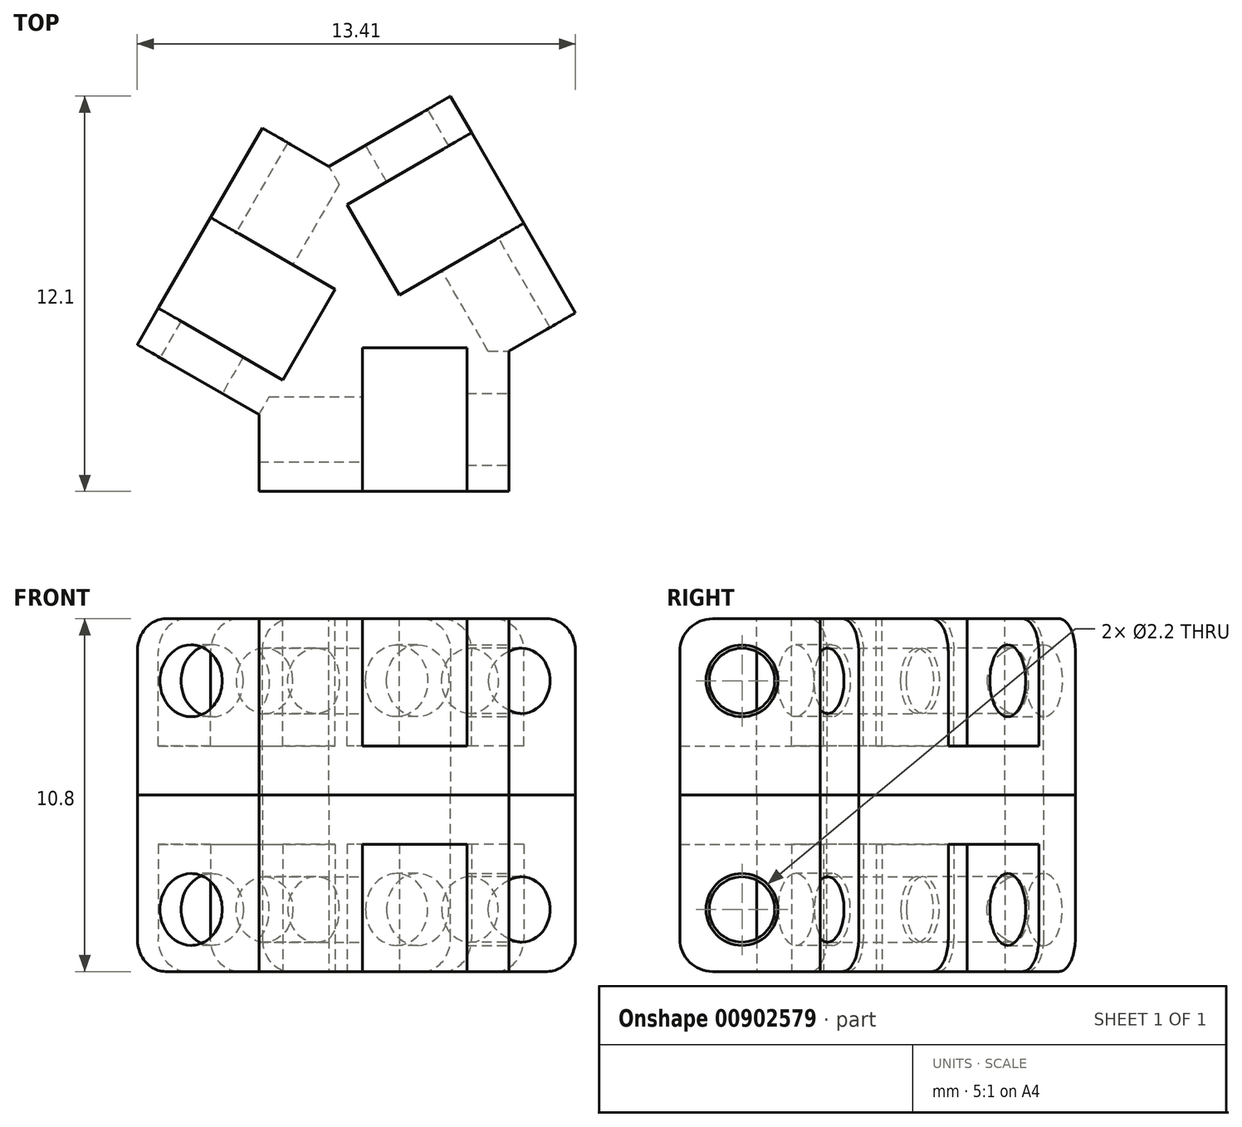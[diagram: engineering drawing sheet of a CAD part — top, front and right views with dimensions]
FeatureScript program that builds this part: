
annotation { "Feature Type Name" : "Feature", "Feature Type Description" : "" }
export const myFeature = defineFeature(function(context is Context, id is Id, definition is map)
    precondition{}
    {
        {
            var Q0;
            Q0=qCreatedBy(makeId("Top.planeOp"),FACE);
            var sketch = newSketch(context, id + "F0", { "sketchPlane" : qUnion([Q0])});
            skLineSegment(sketch, "E0", {"start": v(-2.25, 6.37) * mm, "end": v(-6.64, -1.24) * mm});
            skLineSegment(sketch, "E1", {"start": v(-6.64, -1.24) * mm, "end": v(-4.39, -5.13) * mm});
            skLineSegment(sketch, "E2", {"start": v(-4.39, -5.13) * mm, "end": v(4.39, -5.13) * mm});
            skLineSegment(sketch, "E3", {"start": v(4.39, -5.13) * mm, "end": v(6.64, -1.24) * mm});
            skLineSegment(sketch, "E4", {"start": v(6.64, -1.24) * mm, "end": v(2.25, 6.37) * mm});
            skLineSegment(sketch, "E5", {"start": v(2.25, 6.37) * mm, "end": v(-2.25, 6.37) * mm});
            skLineSegment(sketch, "E6", {"start": v(-5.51, -3.18) * mm, "end": v(4.44, 2.57) * mm, "construction": true});
            skLineSegment(sketch, "E7", {"start": v(0, 6.37) * mm, "end": v(0, -5.13) * mm, "construction": true});
            skSolve(sketch);
        }
        {
            var Q0;
            Q0 = qSketchRegion(id + "F0", true);
            extrude(context, id + "F1", {"entities" : qUnion([Q0]), "depth" : 5 * mm, "offsetDistance" : 25 * mm});
        }
        {
            var Q0;
            Q0=makeQuery(id+"F1.opExtrude","CAP_FACE",FACE,{"disambiguationData":[OSD([sQuery(id+"F0.wireOp",EDGE,"E0"),sQuery(id+"F0.wireOp",EDGE,"E1"),sQuery(id+"F0.wireOp",EDGE,"E2"),sQuery(id+"F0.wireOp",EDGE,"E3"),sQuery(id+"F0.wireOp",EDGE,"E4"),sQuery(id+"F0.wireOp",EDGE,"E5")])],"isStart":false});
            var sketch = newSketch(context, id + "F2", { "sketchPlane" : qUnion([Q0])});
            skLineSegment(sketch, "E8.bottom", {"start": v(-0.1, -5.13) * mm, "end": v(3.1, -5.13) * mm});
            skLineSegment(sketch, "E8.top", {"start": v(-0.1, -1.13) * mm, "end": v(3.1, -1.13) * mm});
            skLineSegment(sketch, "E8.left", {"start": v(-0.1, -5.13) * mm, "end": v(-0.1, -1.13) * mm});
            skLineSegment(sketch, "E8.right", {"start": v(3.1, -5.13) * mm, "end": v(3.1, -1.13) * mm});
            skPoint(sketch, "E9", {"position": v(1.5, -5.13) * mm});
            skLineSegment(sketch, "E10.1.0", {"start": v(2.9, 5.25) * mm, "end": v(-0.57, 3.25) * mm});
            skLineSegment(sketch, "E10.1.1", {"start": v(1.03, 0.48) * mm, "end": v(-0.57, 3.25) * mm});
            skLineSegment(sketch, "E10.1.2", {"start": v(4.5, 2.48) * mm, "end": v(1.03, 0.48) * mm});
            skLineSegment(sketch, "E10.1.3", {"start": v(4.5, 2.48) * mm, "end": v(2.9, 5.25) * mm});
            skLineSegment(sketch, "E10.2.0", {"start": v(-6, -0.12) * mm, "end": v(-2.53, -2.12) * mm});
            skLineSegment(sketch, "E10.2.1", {"start": v(-0.93, 0.65) * mm, "end": v(-2.53, -2.12) * mm});
            skLineSegment(sketch, "E10.2.2", {"start": v(-4.4, 2.65) * mm, "end": v(-0.93, 0.65) * mm});
            skLineSegment(sketch, "E10.2.3", {"start": v(-4.4, 2.65) * mm, "end": v(-6, -0.12) * mm});
            skPoint(sketch, "E10.center", {"position": v(0, 0) * mm});
            skSolve(sketch);
        }
        {
            var Q0;
            Q0 = qSketchRegion(id + "F2", true);
            extrude(context, id + "F3", {"entities" : qUnion([Q0]), "operationType" : NewBodyOperationType.REMOVE, "oppositeDirection" : true, "depth" : 3.5 * mm, "offsetDistance" : 25 * mm});
        }
        {
            var Q0;
            Q0=makeQuery(id+"F1.opExtrude","CAP_FACE",FACE,{"disambiguationData":[OSD([sQuery(id+"F0.wireOp",EDGE,"E0"),sQuery(id+"F0.wireOp",EDGE,"E1"),sQuery(id+"F0.wireOp",EDGE,"E2"),sQuery(id+"F0.wireOp",EDGE,"E3"),sQuery(id+"F0.wireOp",EDGE,"E4"),sQuery(id+"F0.wireOp",EDGE,"E5")])],"isStart":false});
            var sketch = newSketch(context, id + "F4", { "sketchPlane" : qUnion([Q0])});
            skLineSegment(sketch, "E11.bottom", {"start": v(4.39, -5.13) * mm, "end": v(6.64, -5.13) * mm});
            skLineSegment(sketch, "E11.top", {"start": v(4.39, -1.24) * mm, "end": v(6.64, -1.24) * mm});
            skLineSegment(sketch, "E11.left", {"start": v(4.39, -5.13) * mm, "end": v(4.39, -1.24) * mm});
            skLineSegment(sketch, "E11.right", {"start": v(6.64, -5.13) * mm, "end": v(6.64, -1.24) * mm});
            skLineSegment(sketch, "E12.1.0", {"start": v(2.25, 6.37) * mm, "end": v(1.12, 8.32) * mm});
            skLineSegment(sketch, "E12.1.1", {"start": v(-1.12, 4.42) * mm, "end": v(-2.25, 6.37) * mm});
            skLineSegment(sketch, "E12.1.2", {"start": v(2.25, 6.37) * mm, "end": v(-1.13, 4.42) * mm});
            skLineSegment(sketch, "E12.1.3", {"start": v(1.13, 8.32) * mm, "end": v(-2.25, 6.37) * mm});
            skLineSegment(sketch, "E12.2.0", {"start": v(-6.64, -1.24) * mm, "end": v(-7.76, -3.18) * mm});
            skLineSegment(sketch, "E12.2.1", {"start": v(-3.26, -3.18) * mm, "end": v(-4.39, -5.13) * mm});
            skLineSegment(sketch, "E12.2.2", {"start": v(-6.64, -1.24) * mm, "end": v(-3.26, -3.18) * mm});
            skLineSegment(sketch, "E12.2.3", {"start": v(-7.76, -3.18) * mm, "end": v(-4.39, -5.13) * mm});
            skPoint(sketch, "E12.center", {"position": v(0, 0) * mm});
            skSolve(sketch);
        }
        {
            var Q0;
            Q0 = qSketchRegion(id + "F4", true);
            var Q1;
            Q1=makeQuery(id+"F1.opExtrude","CAP_FACE",FACE,{"disambiguationData":[OSD([sQuery(id+"F0.wireOp",EDGE,"E0"),sQuery(id+"F0.wireOp",EDGE,"E1"),sQuery(id+"F0.wireOp",EDGE,"E2"),sQuery(id+"F0.wireOp",EDGE,"E3"),sQuery(id+"F0.wireOp",EDGE,"E4"),sQuery(id+"F0.wireOp",EDGE,"E5")])],"isStart":true});
            extrude(context, id + "F5", {"entities" : qUnion([Q0]), "operationType" : NewBodyOperationType.REMOVE, "endBound" : BoundingType.UP_TO_SURFACE, "oppositeDirection" : true, "depth" : 25 * mm, "endBoundEntityFace" : qUnion([Q1]), "offsetDistance" : 25 * mm});
        }
        {
            var Q0;
            Q0=makeQuery(id+"F5.boolean.opBoolean","COPY",FACE,{"derivedFrom":makeQuery(id+"F5.opExtrude","SWEPT_FACE",FACE,{"disambiguationData":[OSD([sQuery(id+"F4.wireOp",EDGE,"E12.2.2")])]})});
            var sketch = newSketch(context, id + "F6", { "sketchPlane" : qUnion([Q0])});
            skCircle(sketch, "E13", {"center": v(-3.63, 3.5) * mm, "radius": 1.1 * mm});
            skSolve(sketch);
        }
        {
            var Q0;
            Q0=makeQuery(id+"F5.boolean.opBoolean","COPY",FACE,{"derivedFrom":makeQuery(id+"F5.opExtrude","SWEPT_FACE",FACE,{"disambiguationData":[OSD([sQuery(id+"F4.wireOp",EDGE,"E11.left")])]})});
            var sketch = newSketch(context, id + "F7", { "sketchPlane" : qUnion([Q0])});
            skCircle(sketch, "E14", {"center": v(-3.63, 3.5) * mm, "radius": 1.1 * mm});
            skSolve(sketch);
        }
        {
            var Q0;
            Q0=makeQuery(id+"F6.imprint","IMPRINT",FACE,{"disambiguationData":[TD([[makeQuery(id+"F6.imprint","IMPRINT",EDGE,{"derivedFrom":sQuery(id+"F6.wireOp",EDGE,"E13")}),1.0]])]});
            var Q1;
            Q1=makeQuery(id+"F3.boolean.opBoolean","COPY",FACE,{"derivedFrom":makeQuery(id+"F3.opExtrude","SWEPT_FACE",FACE,{"disambiguationData":[OSD([sQuery(id+"F2.wireOp",EDGE,"E10.2.0")])]})});
            extrude(context, id + "F8", {"entities" : qUnion([Q0]), "operationType" : NewBodyOperationType.REMOVE, "endBound" : BoundingType.UP_TO_SURFACE, "oppositeDirection" : true, "depth" : 25 * mm, "endBoundEntityFace" : qUnion([Q1]), "offsetDistance" : 25 * mm});
        }
        {
            var Q0;
            Q0=makeQuery(id+"F5.boolean.opBoolean","COPY",FACE,{"derivedFrom":makeQuery(id+"F5.opExtrude","SWEPT_FACE",FACE,{"disambiguationData":[OSD([sQuery(id+"F4.wireOp",EDGE,"E12.1.2")])]})});
            var sketch = newSketch(context, id + "F9", { "sketchPlane" : qUnion([Q0])});
            skCircle(sketch, "E15", {"center": v(-3.63, 3.5) * mm, "radius": 1.1 * mm});
            skSolve(sketch);
        }
        {
            var Q0;
            Q0 = qSketchRegion(id + "F7", true);
            var Q1;
            Q1=makeQuery(id+"F3.boolean.opBoolean","COPY",FACE,{"derivedFrom":makeQuery(id+"F3.opExtrude","SWEPT_FACE",FACE,{"disambiguationData":[OSD([sQuery(id+"F2.wireOp",EDGE,"E8.right")])]})});
            extrude(context, id + "F10", {"entities" : qUnion([Q0]), "operationType" : NewBodyOperationType.REMOVE, "endBound" : BoundingType.UP_TO_SURFACE, "oppositeDirection" : true, "depth" : 25 * mm, "endBoundEntityFace" : qUnion([Q1]), "offsetDistance" : 25 * mm});
        }
        {
            var Q0;
            Q0 = qSketchRegion(id + "F9", true);
            var Q1;
            Q1=makeQuery(id+"F3.boolean.opBoolean","COPY",FACE,{"derivedFrom":makeQuery(id+"F3.opExtrude","SWEPT_FACE",FACE,{"disambiguationData":[OSD([sQuery(id+"F2.wireOp",EDGE,"E10.1.0")])]})});
            extrude(context, id + "F11", {"entities" : qUnion([Q0]), "operationType" : NewBodyOperationType.REMOVE, "endBound" : BoundingType.UP_TO_SURFACE, "oppositeDirection" : true, "depth" : 25 * mm, "endBoundEntityFace" : qUnion([Q1]), "offsetDistance" : 25 * mm});
        }
        {
            var Q0;
            Q0=makeQuery(id+"F3.boolean.opBoolean","COPY",FACE,{"derivedFrom":makeQuery(id+"F3.opExtrude","SWEPT_FACE",FACE,{"disambiguationData":[OSD([sQuery(id+"F2.wireOp",EDGE,"E8.left")])]})});
            var sketch = newSketch(context, id + "F12", { "sketchPlane" : qUnion([Q0])});
            skCircle(sketch, "E16", {"center": v(-3.63, 3.5) * mm, "radius": 1 * mm});
            skSolve(sketch);
        }
        {
            var Q0;
            Q0=makeQuery(id+"F3.boolean.opBoolean","COPY",FACE,{"derivedFrom":makeQuery(id+"F3.opExtrude","SWEPT_FACE",FACE,{"disambiguationData":[OSD([sQuery(id+"F2.wireOp",EDGE,"E10.1.2")])]})});
            var sketch = newSketch(context, id + "F13", { "sketchPlane" : qUnion([Q0])});
            skCircle(sketch, "E17", {"center": v(-3.63, 3.5) * mm, "radius": 1 * mm});
            skSolve(sketch);
        }
        {
            var Q0;
            Q0=makeQuery(id+"F3.boolean.opBoolean","COPY",FACE,{"derivedFrom":makeQuery(id+"F3.opExtrude","SWEPT_FACE",FACE,{"disambiguationData":[OSD([sQuery(id+"F2.wireOp",EDGE,"E10.2.2")])]})});
            var sketch = newSketch(context, id + "F14", { "sketchPlane" : qUnion([Q0])});
            skCircle(sketch, "E18", {"center": v(-3.63, 3.5) * mm, "radius": 1 * mm});
            skSolve(sketch);
        }
        {
            var Q0;
            Q0 = qSketchRegion(id + "F12", true);
            var Q1;
            Q1=makeQuery(id+"F5.boolean.opBoolean","COPY",FACE,{"derivedFrom":makeQuery(id+"F5.opExtrude","SWEPT_FACE",FACE,{"disambiguationData":[OSD([sQuery(id+"F4.wireOp",EDGE,"E12.2.1")])]})});
            extrude(context, id + "F15", {"entities" : qUnion([Q0]), "operationType" : NewBodyOperationType.REMOVE, "endBound" : BoundingType.UP_TO_SURFACE, "oppositeDirection" : true, "depth" : 25 * mm, "endBoundEntityFace" : qUnion([Q1]), "offsetDistance" : 25 * mm});
        }
        {
            var Q0;
            Q0 = qSketchRegion(id + "F13", true);
            var Q1;
            Q1=makeQuery(id+"F5.boolean.opBoolean","COPY",FACE,{"derivedFrom":makeQuery(id+"F5.opExtrude","SWEPT_FACE",FACE,{"disambiguationData":[OSD([sQuery(id+"F4.wireOp",EDGE,"E11.top")])]})});
            extrude(context, id + "F16", {"entities" : qUnion([Q0]), "operationType" : NewBodyOperationType.REMOVE, "endBound" : BoundingType.UP_TO_SURFACE, "oppositeDirection" : true, "depth" : 25 * mm, "endBoundEntityFace" : qUnion([Q1]), "offsetDistance" : 25 * mm});
        }
        {
            var Q0;
            Q0 = qSketchRegion(id + "F14", true);
            var Q1;
            Q1=makeQuery(id+"F5.boolean.opBoolean","COPY",FACE,{"derivedFrom":makeQuery(id+"F5.opExtrude","SWEPT_FACE",FACE,{"disambiguationData":[OSD([sQuery(id+"F4.wireOp",EDGE,"E12.1.1")])]})});
            extrude(context, id + "F17", {"entities" : qUnion([Q0]), "operationType" : NewBodyOperationType.REMOVE, "endBound" : BoundingType.UP_TO_SURFACE, "oppositeDirection" : true, "depth" : 25 * mm, "endBoundEntityFace" : qUnion([Q1]), "offsetDistance" : 25 * mm});
        }
        {
            var Q0;
            Q0=makeQuery(id+"F1.opExtrude","CAP_FACE",FACE,{"disambiguationData":[OSD([sQuery(id+"F0.wireOp",EDGE,"E0"),sQuery(id+"F0.wireOp",EDGE,"E1"),sQuery(id+"F0.wireOp",EDGE,"E2"),sQuery(id+"F0.wireOp",EDGE,"E3"),sQuery(id+"F0.wireOp",EDGE,"E4"),sQuery(id+"F0.wireOp",EDGE,"E5")])],"isStart":false});
            extrude(context, id + "F18", {"entities" : qUnion([Q0]), "operationType" : NewBodyOperationType.ADD, "depth" : 0.4 * mm, "offsetDistance" : 25 * mm});
        }
        {
            var Q0;
            {var subQ0=sQuery(id+"F0.wireOp",EDGE,"E5");var subQ1=sQuery(id+"F0.wireOp",EDGE,"E4");var subQ2=sQuery(id+"F0.wireOp",EDGE,"E3");var subQ4=makeQuery(id+"F1.opExtrude","SWEPT_FACE",FACE,{"disambiguationData":[OSD([subQ1])]});var subQ5=makeQuery(id+"F1.opExtrude","CAP_EDGE",EDGE,{"disambiguationData":[OSD([subQ1])],"isStart":false});Q0=makeQuery(id+"F18.boolean.opBoolean","MERGE",FACE,{"derivedFrom":[subQ4,makeQuery(id+"F18.opExtrude","SWEPT_FACE",FACE,{"disambiguationData":[OSD([subQ1]),TDD([makeQuery(id+"F3.boolean.opBoolean","SPLIT",EDGE,{"disambiguationData":[TD([makeQuery(id+"F1.opExtrude","SWEPT_FACE",FACE,{"disambiguationData":[OSD([subQ2])]})])],"derivedFrom":subQ5})])]}),makeQuery(id+"F18.opExtrude","SWEPT_FACE",FACE,{"disambiguationData":[OSD([subQ1]),TDD([makeQuery(id+"F3.boolean.opBoolean","SPLIT",EDGE,{"disambiguationData":[TD([makeQuery(id+"F1.opExtrude","SWEPT_FACE",FACE,{"disambiguationData":[OSD([subQ0])]})])],"derivedFrom":subQ5})])]})]});}
            extrude(context, id + "F19", {"entities" : qUnion([Q0]), "operationType" : NewBodyOperationType.ADD, "depth" : 0.4 * mm, "offsetDistance" : 25 * mm});
        }
        {
            var Q0;
            {var subQ0=sQuery(id+"F0.wireOp",EDGE,"E0");var subQ1=makeQuery(id+"F1.opExtrude","SWEPT_FACE",FACE,{"disambiguationData":[OSD([subQ0])]});var subQ2=sQuery(id+"F0.wireOp",EDGE,"E5");var subQ3=sQuery(id+"F0.wireOp",EDGE,"E1");var subQ5=makeQuery(id+"F1.opExtrude","CAP_EDGE",EDGE,{"disambiguationData":[OSD([subQ0])],"isStart":false});Q0=makeQuery(id+"F18.boolean.opBoolean","MERGE",FACE,{"derivedFrom":[subQ1,makeQuery(id+"F18.opExtrude","SWEPT_FACE",FACE,{"disambiguationData":[OSD([subQ0]),TDD([makeQuery(id+"F3.boolean.opBoolean","SPLIT",EDGE,{"disambiguationData":[TD([makeQuery(id+"F1.opExtrude","SWEPT_FACE",FACE,{"disambiguationData":[OSD([subQ2])]})])],"derivedFrom":subQ5})])]}),makeQuery(id+"F18.opExtrude","SWEPT_FACE",FACE,{"disambiguationData":[OSD([subQ0]),TDD([makeQuery(id+"F3.boolean.opBoolean","SPLIT",EDGE,{"disambiguationData":[TD([makeQuery(id+"F1.opExtrude","SWEPT_FACE",FACE,{"disambiguationData":[OSD([subQ3])]})])],"derivedFrom":subQ5})])]})]});}
            extrude(context, id + "F20", {"entities" : qUnion([Q0]), "operationType" : NewBodyOperationType.ADD, "depth" : 0.4 * mm, "offsetDistance" : 25 * mm});
        }
        {
            var Q0;
            {var subQ0=sQuery(id+"F0.wireOp",EDGE,"E3");var subQ1=sQuery(id+"F0.wireOp",EDGE,"E2");var subQ2=sQuery(id+"F0.wireOp",EDGE,"E1");var subQ4=makeQuery(id+"F1.opExtrude","SWEPT_FACE",FACE,{"disambiguationData":[OSD([subQ1])]});var subQ5=makeQuery(id+"F1.opExtrude","CAP_EDGE",EDGE,{"disambiguationData":[OSD([subQ1])],"isStart":false});Q0=makeQuery(id+"F18.boolean.opBoolean","MERGE",FACE,{"derivedFrom":[subQ4,makeQuery(id+"F18.opExtrude","SWEPT_FACE",FACE,{"disambiguationData":[OSD([subQ1]),TDD([makeQuery(id+"F3.boolean.opBoolean","SPLIT",EDGE,{"disambiguationData":[TD([makeQuery(id+"F1.opExtrude","SWEPT_FACE",FACE,{"disambiguationData":[OSD([subQ2])]})])],"derivedFrom":subQ5})])]}),makeQuery(id+"F18.opExtrude","SWEPT_FACE",FACE,{"disambiguationData":[OSD([subQ1]),TDD([makeQuery(id+"F3.boolean.opBoolean","SPLIT",EDGE,{"disambiguationData":[TD([makeQuery(id+"F1.opExtrude","SWEPT_FACE",FACE,{"disambiguationData":[OSD([subQ0])]})])],"derivedFrom":subQ5})])]})]});}
            extrude(context, id + "F21", {"entities" : qUnion([Q0]), "operationType" : NewBodyOperationType.ADD, "depth" : 0.4 * mm, "offsetDistance" : 25 * mm});
        }
        {
            var Q0;
            {var subQ0=sQuery(id+"F0.wireOp",EDGE,"E5");var subQ1=sQuery(id+"F0.wireOp",EDGE,"E4");var subQ2=sQuery(id+"F0.wireOp",EDGE,"E3");var subQ3=sQuery(id+"F0.wireOp",EDGE,"E2");var subQ4=sQuery(id+"F0.wireOp",EDGE,"E1");var subQ5=sQuery(id+"F0.wireOp",EDGE,"E0");var subQ8=makeQuery(id+"F1.opExtrude","SWEPT_FACE",FACE,{"disambiguationData":[OSD([subQ2])]});var subQ9=makeQuery(id+"F1.opExtrude","CAP_EDGE",EDGE,{"disambiguationData":[OSD([subQ3])],"isStart":false});var subQ10=makeQuery(id+"F1.opExtrude","SWEPT_FACE",FACE,{"disambiguationData":[OSD([subQ4])]});var subQ12=makeQuery(id+"F1.opExtrude","CAP_EDGE",EDGE,{"disambiguationData":[OSD([subQ5])],"isStart":false});var subQ13=makeQuery(id+"F1.opExtrude","SWEPT_FACE",FACE,{"disambiguationData":[OSD([subQ0])]});var subQ15=makeQuery(id+"F1.opExtrude","CAP_EDGE",EDGE,{"disambiguationData":[OSD([subQ1])],"isStart":false});Q0=makeQuery(id+"F21.boolean.opBoolean","MERGE",FACE,{"derivedFrom":[makeQuery(id+"F20.boolean.opBoolean","MERGE",FACE,{"derivedFrom":[makeQuery(id+"F19.boolean.opBoolean","MERGE",FACE,{"derivedFrom":[makeQuery(id+"F18.opExtrude","CAP_FACE",FACE,{"disambiguationData":[OSD([subQ5,subQ4,subQ3,subQ2,subQ1,subQ0])],"isStart":false}),makeQuery(id+"F19.opExtrude","SWEPT_FACE",FACE,{"disambiguationData":[OSD([subQ1]),TDD([makeQuery(id+"F18.opExtrude","CAP_EDGE",EDGE,{"disambiguationData":[OSD([subQ1]),TDD([makeQuery(id+"F3.boolean.opBoolean","SPLIT",EDGE,{"disambiguationData":[TD([subQ8])],"derivedFrom":subQ15})])],"isStart":false})])]}),makeQuery(id+"F19.opExtrude","SWEPT_FACE",FACE,{"disambiguationData":[OSD([subQ1]),TDD([makeQuery(id+"F18.opExtrude","CAP_EDGE",EDGE,{"disambiguationData":[OSD([subQ1]),TDD([makeQuery(id+"F3.boolean.opBoolean","SPLIT",EDGE,{"disambiguationData":[TD([subQ13])],"derivedFrom":subQ15})])],"isStart":false})])]})]}),makeQuery(id+"F20.opExtrude","SWEPT_FACE",FACE,{"disambiguationData":[OSD([subQ5]),TDD([makeQuery(id+"F18.opExtrude","CAP_EDGE",EDGE,{"disambiguationData":[OSD([subQ5]),TDD([makeQuery(id+"F3.boolean.opBoolean","SPLIT",EDGE,{"disambiguationData":[TD([subQ13])],"derivedFrom":subQ12})])],"isStart":false})])]}),makeQuery(id+"F20.opExtrude","SWEPT_FACE",FACE,{"disambiguationData":[OSD([subQ5]),TDD([makeQuery(id+"F18.opExtrude","CAP_EDGE",EDGE,{"disambiguationData":[OSD([subQ5]),TDD([makeQuery(id+"F3.boolean.opBoolean","SPLIT",EDGE,{"disambiguationData":[TD([subQ10])],"derivedFrom":subQ12})])],"isStart":false})])]})]}),makeQuery(id+"F21.opExtrude","SWEPT_FACE",FACE,{"disambiguationData":[OSD([subQ3]),TDD([makeQuery(id+"F18.opExtrude","CAP_EDGE",EDGE,{"disambiguationData":[OSD([subQ3]),TDD([makeQuery(id+"F3.boolean.opBoolean","SPLIT",EDGE,{"disambiguationData":[TD([subQ10])],"derivedFrom":subQ9})])],"isStart":false})])]}),makeQuery(id+"F21.opExtrude","SWEPT_FACE",FACE,{"disambiguationData":[OSD([subQ3]),TDD([makeQuery(id+"F18.opExtrude","CAP_EDGE",EDGE,{"disambiguationData":[OSD([subQ3]),TDD([makeQuery(id+"F3.boolean.opBoolean","SPLIT",EDGE,{"disambiguationData":[TD([subQ8])],"derivedFrom":subQ9})])],"isStart":false})])]})]});}
            var sketch = newSketch(context, id + "F22", { "sketchPlane" : qUnion([Q0])});
            skLineSegment(sketch, "E19.bottom", {"start": v(-3.26, -3.18) * mm, "end": v(-4.39, -3.18) * mm});
            skLineSegment(sketch, "E19.top", {"start": v(-3.26, -5.53) * mm, "end": v(-4.39, -5.53) * mm});
            skLineSegment(sketch, "E19.left", {"start": v(-3.26, -3.18) * mm, "end": v(-3.26, -5.53) * mm});
            skLineSegment(sketch, "E19.right", {"start": v(-4.39, -3.18) * mm, "end": v(-4.39, -5.53) * mm});
            skLineSegment(sketch, "E20.1.0", {"start": v(4.39, -1.24) * mm, "end": v(4.95, -2.2) * mm});
            skLineSegment(sketch, "E20.1.1", {"start": v(4.95, -2.2) * mm, "end": v(6.99, -1.04) * mm});
            skLineSegment(sketch, "E20.1.2", {"start": v(4.39, -1.24) * mm, "end": v(6.42, -0.06) * mm});
            skLineSegment(sketch, "E20.1.3", {"start": v(6.42, -0.06) * mm, "end": v(6.99, -1.04) * mm});
            skLineSegment(sketch, "E20.2.0", {"start": v(-1.12, 4.42) * mm, "end": v(-0.56, 5.4) * mm});
            skLineSegment(sketch, "E20.2.1", {"start": v(-0.56, 5.4) * mm, "end": v(-2.6, 6.57) * mm});
            skLineSegment(sketch, "E20.2.2", {"start": v(-1.12, 4.42) * mm, "end": v(-3.16, 5.6) * mm});
            skLineSegment(sketch, "E20.2.3", {"start": v(-3.16, 5.6) * mm, "end": v(-2.6, 6.57) * mm});
            skPoint(sketch, "E20.center", {"position": v(0, 0) * mm});
            skSolve(sketch);
        }
        {
            var Q0;
            Q0 = qSketchRegion(id + "F22", true);
            var Q1;
            {var subQ0=sQuery(id+"F0.wireOp",EDGE,"E2");var subQ1=sQuery(id+"F0.wireOp",EDGE,"E0");var subQ2=sQuery(id+"F0.wireOp",EDGE,"E4");Q1=makeQuery(id+"F21.boolean.opBoolean","MERGE",FACE,{"derivedFrom":[makeQuery(id+"F20.boolean.opBoolean","MERGE",FACE,{"derivedFrom":[makeQuery(id+"F19.boolean.opBoolean","MERGE",FACE,{"derivedFrom":[makeQuery(id+"F1.opExtrude","CAP_FACE",FACE,{"disambiguationData":[OSD([subQ1,sQuery(id+"F0.wireOp",EDGE,"E1"),subQ0,sQuery(id+"F0.wireOp",EDGE,"E3"),subQ2,sQuery(id+"F0.wireOp",EDGE,"E5")])],"isStart":true}),makeQuery(id+"F19.opExtrude","SWEPT_FACE",FACE,{"disambiguationData":[OSD([subQ2]),TDD([makeQuery(id+"F1.opExtrude","CAP_EDGE",EDGE,{"disambiguationData":[OSD([subQ2])],"isStart":true})])]})]}),makeQuery(id+"F20.opExtrude","SWEPT_FACE",FACE,{"disambiguationData":[OSD([subQ1]),TDD([makeQuery(id+"F1.opExtrude","CAP_EDGE",EDGE,{"disambiguationData":[OSD([subQ1])],"isStart":true})])]})]}),makeQuery(id+"F21.opExtrude","SWEPT_FACE",FACE,{"disambiguationData":[OSD([subQ0]),TDD([makeQuery(id+"F1.opExtrude","CAP_EDGE",EDGE,{"disambiguationData":[OSD([subQ0])],"isStart":true})])]})]});}
            extrude(context, id + "F23", {"entities" : qUnion([Q0]), "operationType" : NewBodyOperationType.REMOVE, "endBound" : BoundingType.UP_TO_SURFACE, "oppositeDirection" : true, "depth" : 25 * mm, "endBoundEntityFace" : qUnion([Q1]), "offsetDistance" : 25 * mm});
        }
        {
            var Q0;
            {var subQ0=sQuery(id+"F0.wireOp",EDGE,"E2");var subQ1=sQuery(id+"F0.wireOp",EDGE,"E1");Q0=makeQuery(id+"F21.opExtrude","CAP_EDGE",EDGE,{"disambiguationData":[OSD([subQ0]),TDD([makeQuery(id+"F18.opExtrude","CAP_EDGE",EDGE,{"disambiguationData":[OSD([subQ0]),TDD([makeQuery(id+"F3.boolean.opBoolean","SPLIT",EDGE,{"disambiguationData":[TD([makeQuery(id+"F1.opExtrude","SWEPT_FACE",FACE,{"disambiguationData":[OSD([subQ1])]})])],"derivedFrom":makeQuery(id+"F1.opExtrude","CAP_EDGE",EDGE,{"disambiguationData":[OSD([subQ0])],"isStart":false})})])],"isStart":false})])],"isStart":false});}
            var Q1;
            {var subQ0=sQuery(id+"F0.wireOp",EDGE,"E3");var subQ1=sQuery(id+"F0.wireOp",EDGE,"E2");Q1=makeQuery(id+"F21.opExtrude","CAP_EDGE",EDGE,{"disambiguationData":[OSD([subQ1]),TDD([makeQuery(id+"F18.opExtrude","CAP_EDGE",EDGE,{"disambiguationData":[OSD([subQ1]),TDD([makeQuery(id+"F3.boolean.opBoolean","SPLIT",EDGE,{"disambiguationData":[TD([makeQuery(id+"F1.opExtrude","SWEPT_FACE",FACE,{"disambiguationData":[OSD([subQ0])]})])],"derivedFrom":makeQuery(id+"F1.opExtrude","CAP_EDGE",EDGE,{"disambiguationData":[OSD([subQ1])],"isStart":false})})])],"isStart":false})])],"isStart":false});}
            var Q2;
            {var subQ0=sQuery(id+"F0.wireOp",EDGE,"E4");var subQ1=sQuery(id+"F0.wireOp",EDGE,"E3");Q2=makeQuery(id+"F19.opExtrude","CAP_EDGE",EDGE,{"disambiguationData":[OSD([subQ0]),TDD([makeQuery(id+"F18.opExtrude","CAP_EDGE",EDGE,{"disambiguationData":[OSD([subQ0]),TDD([makeQuery(id+"F3.boolean.opBoolean","SPLIT",EDGE,{"disambiguationData":[TD([makeQuery(id+"F1.opExtrude","SWEPT_FACE",FACE,{"disambiguationData":[OSD([subQ1])]})])],"derivedFrom":makeQuery(id+"F1.opExtrude","CAP_EDGE",EDGE,{"disambiguationData":[OSD([subQ0])],"isStart":false})})])],"isStart":false})])],"isStart":false});}
            var Q3;
            {var subQ0=sQuery(id+"F0.wireOp",EDGE,"E5");var subQ1=sQuery(id+"F0.wireOp",EDGE,"E4");Q3=makeQuery(id+"F19.opExtrude","CAP_EDGE",EDGE,{"disambiguationData":[OSD([subQ1]),TDD([makeQuery(id+"F18.opExtrude","CAP_EDGE",EDGE,{"disambiguationData":[OSD([subQ1]),TDD([makeQuery(id+"F3.boolean.opBoolean","SPLIT",EDGE,{"disambiguationData":[TD([makeQuery(id+"F1.opExtrude","SWEPT_FACE",FACE,{"disambiguationData":[OSD([subQ0])]})])],"derivedFrom":makeQuery(id+"F1.opExtrude","CAP_EDGE",EDGE,{"disambiguationData":[OSD([subQ1])],"isStart":false})})])],"isStart":false})])],"isStart":false});}
            var Q4;
            {var subQ0=sQuery(id+"F0.wireOp",EDGE,"E0");var subQ1=sQuery(id+"F0.wireOp",EDGE,"E5");Q4=makeQuery(id+"F20.opExtrude","CAP_EDGE",EDGE,{"disambiguationData":[OSD([subQ0]),TDD([makeQuery(id+"F18.opExtrude","CAP_EDGE",EDGE,{"disambiguationData":[OSD([subQ0]),TDD([makeQuery(id+"F3.boolean.opBoolean","SPLIT",EDGE,{"disambiguationData":[TD([makeQuery(id+"F1.opExtrude","SWEPT_FACE",FACE,{"disambiguationData":[OSD([subQ1])]})])],"derivedFrom":makeQuery(id+"F1.opExtrude","CAP_EDGE",EDGE,{"disambiguationData":[OSD([subQ0])],"isStart":false})})])],"isStart":false})])],"isStart":false});}
            var Q5;
            {var subQ0=sQuery(id+"F0.wireOp",EDGE,"E0");var subQ1=sQuery(id+"F0.wireOp",EDGE,"E1");Q5=makeQuery(id+"F20.opExtrude","CAP_EDGE",EDGE,{"disambiguationData":[OSD([subQ0]),TDD([makeQuery(id+"F18.opExtrude","CAP_EDGE",EDGE,{"disambiguationData":[OSD([subQ0]),TDD([makeQuery(id+"F3.boolean.opBoolean","SPLIT",EDGE,{"disambiguationData":[TD([makeQuery(id+"F1.opExtrude","SWEPT_FACE",FACE,{"disambiguationData":[OSD([subQ1])]})])],"derivedFrom":makeQuery(id+"F1.opExtrude","CAP_EDGE",EDGE,{"disambiguationData":[OSD([subQ0])],"isStart":false})})])],"isStart":false})])],"isStart":false});}
            fillet(context, id + "F24", {"entities" : qUnion([Q0, Q1, Q2, Q3, Q4, Q5]), "radius" : 1 * mm, "tangentPropagation" : true, "allowEdgeOverflow" : false});
        }
        {
            var Q0;
            Q0=makeQuery(id+"F1.opExtrude","SWEPT_BODY",BODY,{"disambiguationData":[OSD([sQuery(id+"F0.wireOp",EDGE,"E0"),sQuery(id+"F0.wireOp",EDGE,"E1"),sQuery(id+"F0.wireOp",EDGE,"E2"),sQuery(id+"F0.wireOp",EDGE,"E3"),sQuery(id+"F0.wireOp",EDGE,"E4"),sQuery(id+"F0.wireOp",EDGE,"E5")])]});
            var Q1;
            Q1=qCreatedBy(makeId("Top.planeOp"),FACE);
            mirror(context, id + "F25", {"entities" : qUnion([Q0]), "mirrorPlane" : qUnion([Q1])});
        }
    });
